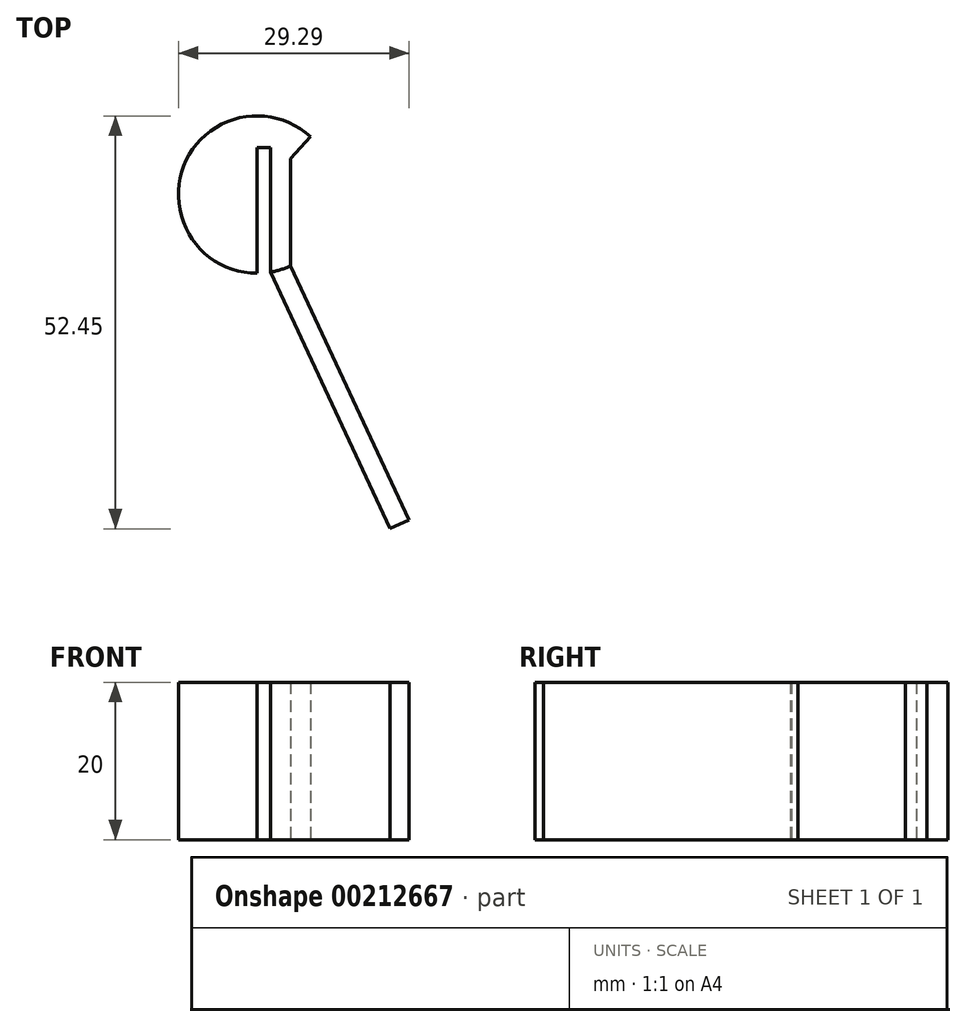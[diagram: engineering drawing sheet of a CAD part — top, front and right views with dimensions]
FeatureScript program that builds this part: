
annotation { "Feature Type Name" : "Feature", "Feature Type Description" : "" }
export const myFeature = defineFeature(function(context is Context, id is Id, definition is map)
    precondition{}
    {
        {
            var Q0;
            Q0=qCreatedBy(makeId("Top.planeOp"),FACE);
            var sketch = newSketch(context, id + "F0", { "sketchPlane" : qUnion([Q0])});
            skArc(sketch, "E0", {"start": v(6.78, 7.35) * mm, "mid": v(-9.31, 3.64) * mm, "end": v(0, -10) * mm});
            skLineSegment(sketch, "E1", {"start": v(0, -10) * mm, "end": v(0, 6) * mm});
            skLineSegment(sketch, "E2", {"start": v(0, 6) * mm, "end": v(1.7, 6) * mm});
            skLineSegment(sketch, "E3", {"start": v(1.7, 6) * mm, "end": v(1.7, -9.85) * mm});
            skLineSegment(sketch, "E4", {"start": v(4.24, 4.6) * mm, "end": v(6.78, 7.35) * mm});
            skLineSegment(sketch, "E5", {"start": v(4.24, 4.6) * mm, "end": v(4.24, -9.06) * mm});
            skPoint(sketch, "E6.orphan", {"position": v(1.7, 1.84) * mm});
            skArc(sketch, "E7.trimOffspring", {"start": v(1.7, -9.85) * mm, "mid": v(3, -9.54) * mm, "end": v(4.24, -9.06) * mm});
            skLineSegment(sketch, "E8", {"start": v(0, 0) * mm, "end": v(0, -34.62) * mm, "construction": true});
            skLineSegment(sketch, "E9", {"start": v(1.7, -9.85) * mm, "end": v(16.9, -42.45) * mm});
            skLineSegment(sketch, "E10", {"start": v(16.9, -42.45) * mm, "end": v(19.3, -41.33) * mm});
            skLineSegment(sketch, "E11", {"start": v(4.24, -9.06) * mm, "end": v(19.3, -41.33) * mm});
            skSolve(sketch);
        }
        {
            var Q0;
            Q0=makeQuery(id+"F0.imprint","IMPRINT",FACE,{"disambiguationData":[TD([[makeQuery(id+"F0.imprint","IMPRINT",EDGE,{"derivedFrom":sQuery(id+"F0.wireOp",EDGE,"E7.trimOffspring")}),-1.0]])]});
            extrude(context, id + "F1", {"entities" : qUnion([Q0]), "depth" : 20 * mm});
        }
        {
            var Q0;
            Q0=makeQuery(id+"F0.imprint","IMPRINT",FACE,{"disambiguationData":[TD([[makeQuery(id+"F0.imprint","IMPRINT",EDGE,{"derivedFrom":sQuery(id+"F0.wireOp",EDGE,"E0")}),1.0]])]});
            extrude(context, id + "F2", {"entities" : qUnion([Q0]), "depth" : 20 * mm});
        }
    });
